# Revit family: Toilet-Bidet-DXV-AT200LS_SpaLet-D29030CS416-415
name_source: partatom
category: Plumbing Fixtures
revit_build: Autodesk Revit 2018 (Build: 20170223_1515(x64)
units: mm (PartAtom-declared; Revit-internal decimal feet)

## family parameters
Always vertical = No
Cut with Voids When Loaded = No
OmniClass Number = 23.45.05.21.11
OmniClass Title = Water Closets
Part Type = Normal
Room Calculation Point = No
Round Connector Dimension = Use Radius
Shared = Yes
Work Plane-Based = Yes

## types (1)
- D29030CS416-415
    ADA Compliant = Yes
    Assembly Code = D2010110
    Bowl Shape = Elongated
    CW Connection = Yes
    CWFU = 5
    Cold Water Connection Diameter = 1/2"
    Cold Water Connection Height = 5 5/16"
    Cold Water Connection Radius = 1/4"
    Cold Water Connection Width = 9 1/16"
    Default Elevation = 0"
    Description = AT200LS SpaLet Integrated Electronic Bidet Toilet
    Electrical Connection Height = 10"
    Electrical Connection Width = 9 1/16"
    Finish = Vitreous_China-DXV-415-Canvas_White
    Flush Rate = 1.32-0.92 gpf (4.9-3.4 lpf)
    Frequency = 60 Hz
    HW Connection = No
    HWFU = 0
    Height = 19 5/16"
    IAPMO Compliance = Meets or Exceeds ASME A112.19.2 / CSA B45.1, ASME A112.4.2 / CSA B45.16, UL 1431, CSA C22.2 No. 68-14 Update No. 3, CSA C22.2 No. 64-14EPA WaterSense® Certified
    Installation Type = Floor Mounted
    Length = 26 9/16"
    Manufacturer = DXV
    Material = Vitreous_China-DXV-415-Canvas_White
    Model = D29030CS416-415
    Price = Prices may vary. Please consult Manufacturer Representative for most up-to-date price list.
    Product Documentation Link = https://dxv01.blob.core.windows.net
    Product Page URL = https://www.dxv.com
    Revised Date = 04/05/2021
    URL = http://www.dxv.com
    Vent Connection = No
    Voltage = 120 V
    WFU = 5
    Warranty Documentation Link = https://www.dxv.com
    Warranty Information = 3 year warranty for residential , 2 year warranty for commercial.
    Waste Connection = Yes
    Waste Connection Diameter = 2"
    Waste Connection Radius = 1"
    Width = 14 3/4"

## geometry (parser evidence)
native form markers: Sweep x2
no freeform markers — native parametric forms only
